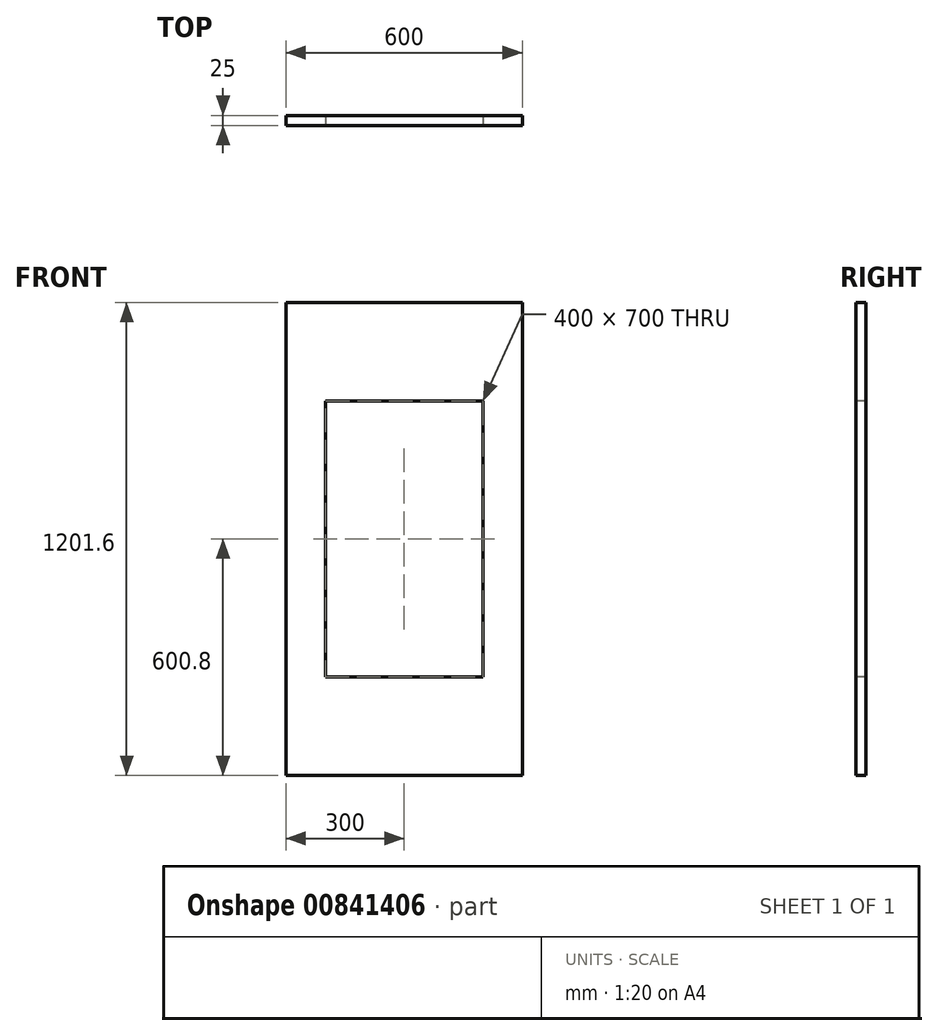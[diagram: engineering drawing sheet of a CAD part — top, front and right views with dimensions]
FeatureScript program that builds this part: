
annotation { "Feature Type Name" : "Feature", "Feature Type Description" : "" }
export const myFeature = defineFeature(function(context is Context, id is Id, definition is map)
    precondition{}
    {
        {
            var Q0;
            Q0=qCreatedBy(makeId("Front.planeOp"),FACE);
            var sketch = newSketch(context, id + "F0", { "sketchPlane" : qUnion([Q0])});
            skLineSegment(sketch, "E0.bottom", {"start": v(300, 600.8) * mm, "end": v(-300, 600.8) * mm});
            skLineSegment(sketch, "E0.top", {"start": v(300, -600.8) * mm, "end": v(-300, -600.8) * mm});
            skLineSegment(sketch, "E0.left", {"start": v(300, 600.8) * mm, "end": v(300, -600.8) * mm});
            skLineSegment(sketch, "E0.right", {"start": v(-300, 600.8) * mm, "end": v(-300, -600.8) * mm});
            skPoint(sketch, "E0.middle", {"position": v(0, 0) * mm});
            skSolve(sketch);
        }
        {
            var Q0;
            Q0=qSketchRegion(id+"F0",true);
            extrude(context, id + "F1", {"entities" : qUnion([Q0]), "depth" : 25 * mm, "offsetDistance" : 25 * mm});
        }
        {
            var Q0;
            Q0=makeQuery(id+"F1.opExtrude","CAP_FACE",FACE,{"disambiguationData":[OSD([sQuery(id+"F0.wireOp",EDGE,"E0.bottom"),sQuery(id+"F0.wireOp",EDGE,"E0.top"),sQuery(id+"F0.wireOp",EDGE,"E0.left"),sQuery(id+"F0.wireOp",EDGE,"E0.right")])],"isStart":false});
            var sketch = newSketch(context, id + "F2", { "sketchPlane" : qUnion([Q0])});
            skLineSegment(sketch, "E1.bottom", {"start": v(200, 350) * mm, "end": v(-200, 350) * mm});
            skLineSegment(sketch, "E1.top", {"start": v(200, -350) * mm, "end": v(-200, -350) * mm});
            skLineSegment(sketch, "E1.left", {"start": v(200, 350) * mm, "end": v(200, -350) * mm});
            skLineSegment(sketch, "E1.right", {"start": v(-200, 350) * mm, "end": v(-200, -350) * mm});
            skPoint(sketch, "E1.middle", {"position": v(0, 0) * mm});
            skSolve(sketch);
        }
        {
            var Q0;
            Q0=makeQuery(id+"F2.imprint","IMPRINT",FACE,{"disambiguationData":[TD([[makeQuery(id+"F2.imprint","IMPRINT",EDGE,{"derivedFrom":sQuery(id+"F2.wireOp",EDGE,"E1.bottom")}),1.0]])]});
            extrude(context, id + "F3", {"entities" : qUnion([Q0]), "operationType" : NewBodyOperationType.REMOVE, "oppositeDirection" : true, "depth" : 857 * mm, "offsetDistance" : 25 * mm});
        }
    });
